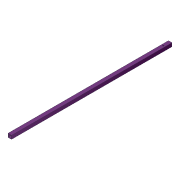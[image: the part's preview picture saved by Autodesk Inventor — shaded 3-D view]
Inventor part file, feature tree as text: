
AUTODESK INVENTOR PART (.ipt)
format: ipt  version: 2012 (Build 160160000, 160)  size: 81,920 bytes
history: native  units: in
note: dims shown in document units (in); Inventor stores cm internally (conversion verified against a paired STEP export)
features: extrude x2, sketch x2, shell x1
ambient origin geometry x8: Origin, YZ Plane, XZ Plane, XY Plane, X Axis, Y Axis, Z Axis, Center Point
bodies: Solid1 (feature_tree)
feature tree (5):
  extrude  "Extrusion1"  Depth=0.5in
  shell  "Shell1"  Thickness=23.0in
  extrude  "Extrusion2"  Depth=0.192in
  sketch  "Sketch1"  dims[d0=0.5in d1=0.5in d2=23.0in d3=0.0in]
  sketch  "Sketch2"  dims[d4=0.0625in d5=0.192in d6=0.25in d7=1.0in d8=1.0in d9=0.0in]
